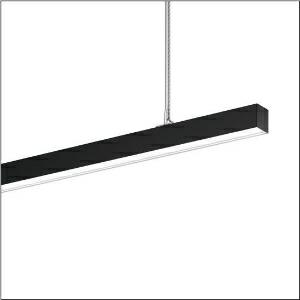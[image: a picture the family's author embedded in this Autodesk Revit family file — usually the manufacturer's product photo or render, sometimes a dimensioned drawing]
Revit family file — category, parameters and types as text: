
# Revit family: silica_r__21_51mx30tct9b_d278
name_source: partatom
category: Lighting Fixtures
units: mm (PartAtom-declared; Revit-internal decimal feet)

## family parameters
Cut with Voids When Loaded = No
Host = Face
Light Source = No
Part Type = Normal
Room Calculation Point = No
Round Connector Dimension = Use Diameter
Shared = No

## types (1)
- --- (1 x LED, 10300 lm, 84.4 W, 6500K)
    Apparent Load = 84 VA
    CIE Flux Codes = 47 79 96 58 100
    Color Rendering = 80
    Color Temperature = 6500K
    Default Elevation = 1800 mm
    Description = Silica® 21, office luminaire, primary optical cover: cover, of PMMA, opal, light emission: direct/indirect distribution, primary light characteristic: symmetric, installation type: suspended mounting, LED, rated luminous flux: 10.300lm, luminous efficacy: 116lm/W, light colour: 8tw, colour temperature: 2700..6500K, control gear: ECG DALI, with terminal, 3+2-pole, max. 2.5mm², mains connection: 220..240V, AC, 50/60Hz, rated input power: 88.7W, luminaire housing, of aluminium, jet black (RAL 9005), length: 3.004mm, width: 53mm, height: 53mm, protection rating (complete): IP20, insulation class (complete): insulation class I (protective earthing), certification: CE, permissible operating ambient temperature: 0..+35°C, standard: EN 50419, packaging unit: 1 piece
    Height = 53 mm
    Lamp = 1 x LED
    Lamp Light Flux = 10300 lm
    Lamp Power = 84.4 W
    Lamp count = 1
    Length = 3004 mm
    Luminous efficacy = 122 lm/W
    Manufacturer = Siteco
    ModVariant = No
    Model = 51MX30TCT9B
    Mounting Place = Ceiling
    Mounting Type = Pendant
    Number of Poles = 1
    OnlyDefault = Yes
    Power Factor = 1
    Product Name = Silica® 21
    Product group = office luminaire | ceiling pendant
    ProductGroupID = 905
    Protection Class = Protection class I
    Protection Degree = IP 20
    RLX_Detail_Level = 1
    RlxData = <blob elided: 22793 chars, md5=60e6c212>
    Socket = socket
    Standby Power = 0 W
    System Light Flux = 10300 lm
    System Power = 84 W
    Type Comments = individual setting
    Type Image = l_1251735.jpg
    URL = http://relux.com
    VarID = @adj_045717
    Voltage = 0 V
    Weight = 0.00 kg
    Width = 53 mm

## geometry (parser evidence)
native form markers: Blend x4, Sweep x11
no freeform markers — native parametric forms only
